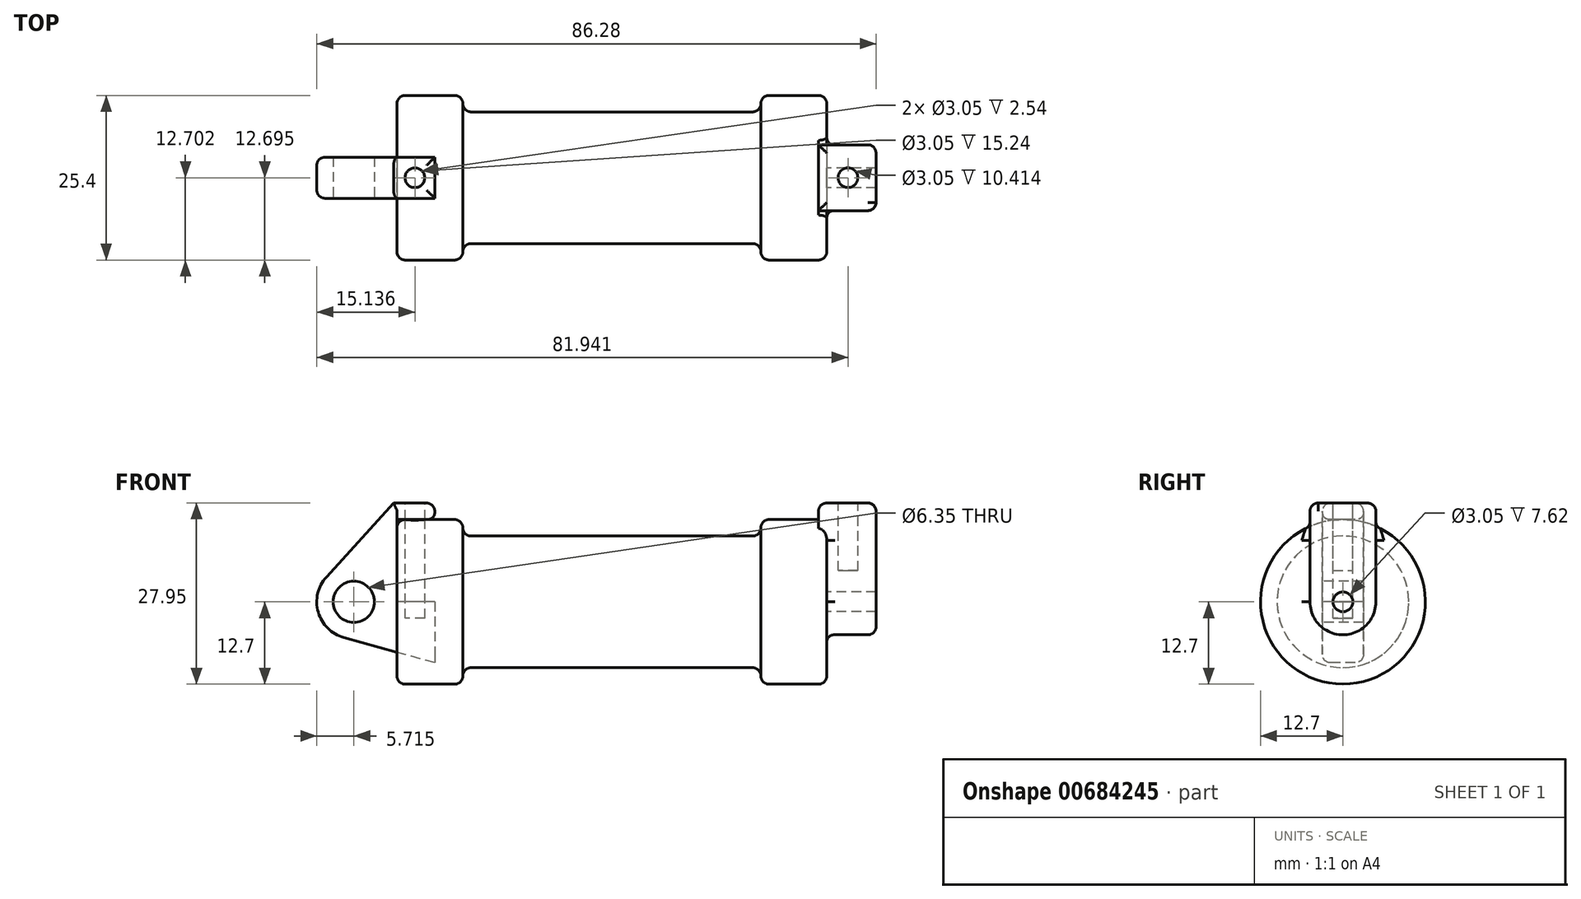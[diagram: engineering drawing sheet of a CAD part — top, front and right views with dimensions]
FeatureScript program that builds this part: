
annotation { "Feature Type Name" : "Feature", "Feature Type Description" : "" }
export const myFeature = defineFeature(function(context is Context, id is Id, definition is map)
    precondition{}
    {
        {
            var Q0;
            Q0=qCreatedBy(makeId("Front.planeOp"),FACE);
            var sketch = newSketch(context, id + "F0", { "sketchPlane" : qUnion([Q0])});
            skLineSegment(sketch, "E0", {"start": v(0, 0) * mm, "end": v(0, 12.7) * mm});
            skLineSegment(sketch, "E1", {"start": v(0, 12.7) * mm, "end": v(10.16, 12.7) * mm});
            skLineSegment(sketch, "E2", {"start": v(10.16, 12.7) * mm, "end": v(10.16, 10.16) * mm});
            skLineSegment(sketch, "E3", {"start": v(10.16, 10.16) * mm, "end": v(56.13, 10.16) * mm});
            skLineSegment(sketch, "E4", {"start": v(56.13, 10.16) * mm, "end": v(56.13, 12.7) * mm});
            skLineSegment(sketch, "E5", {"start": v(56.13, 12.7) * mm, "end": v(66.3, 12.7) * mm});
            skLineSegment(sketch, "E6", {"start": v(66.3, 12.7) * mm, "end": v(66.3, 0) * mm});
            skLineSegment(sketch, "E7", {"start": v(66.3, 0) * mm, "end": v(0, 0) * mm});
            skLineSegment(sketch, "E8", {"start": v(5.84, 15.24) * mm, "end": v(-0.5, 15.24) * mm});
            skLineSegment(sketch, "E9", {"start": v(-0.5, 15.24) * mm, "end": v(-10.88, 3.85) * mm});
            skLineSegment(sketch, "E10", {"start": v(0, 0) * mm, "end": v(-6.65, 0) * mm});
            skCircle(sketch, "E11", {"center": v(-6.65, 0) * mm, "radius": 5.72 * mm});
            skCircle(sketch, "E12", {"center": v(-6.65, 0) * mm, "radius": 3.18 * mm});
            skLineSegment(sketch, "E13", {"start": v(5.84, 15.24) * mm, "end": v(5.84, -9.4) * mm});
            skLineSegment(sketch, "E14", {"start": v(5.84, -9.4) * mm, "end": v(-8.18, -5.5) * mm});
            skSolve(sketch);
        }
        {
            var Q0;
            {var subQ0=sQuery(id+"F0.wireOp",EDGE,"E2");Q0=makeQuery(id+"F0.imprint","IMPRINT",FACE,{"disambiguationData":[TD([[makeQuery(id+"F0.imprint","IMPRINT",EDGE,{"derivedFrom":subQ0}),-1.0]])]});}
            var Q1;
            {var subQ0=sQuery(id+"F0.wireOp",EDGE,"E0");Q1=makeQuery(id+"F0.imprint","IMPRINT",FACE,{"disambiguationData":[TD([[makeQuery(id+"F0.imprint","IMPRINT",EDGE,{"derivedFrom":subQ0}),-1.0]])]});}
            var Q2;
            Q2=sQuery(id+"F0.wireOp",EDGE,"E7");
            revolve(context, id + "F1", {"entities" : qUnion([Q0, Q1]), "axis" : qUnion([Q2]), "revolveType" : RevolveType.FULL});
        }
        {
            var Q0;
            {var subQ1=sQuery(id+"F0.wireOp",EDGE,"E0");Q0=makeQuery(id+"F0.imprint","IMPRINT",FACE,{"disambiguationData":[TD([[makeQuery(id+"F0.imprint","IMPRINT",EDGE,{"derivedFrom":subQ1}),1.0]])]});}
            var Q1;
            {var subQ0=sQuery(id+"F0.wireOp",EDGE,"E14");Q1=makeQuery(id+"F0.imprint","IMPRINT",FACE,{"disambiguationData":[TD([[makeQuery(id+"F0.imprint","IMPRINT",EDGE,{"derivedFrom":subQ0}),-1.0]])]});}
            var Q2;
            {var subQ5=sQuery(id+"F0.wireOp",EDGE,"E12");Q2=makeQuery(id+"F0.imprint","IMPRINT",FACE,{"disambiguationData":[TD([[makeQuery(id+"F0.imprint","IMPRINT",EDGE,{"derivedFrom":subQ5}),-1.0]])]});}
            extrude(context, id + "F2", {"entities" : qUnion([Q0, Q1, Q2]), "endBound" : BoundingType.SYMMETRIC, "oppositeDirection" : true, "depth" : 6.35 * mm, "offsetDistance" : 25.4 * mm});
        }
        {
            var Q0;
            Q0=makeQuery(id+"F1.opRevolve","SWEPT_FACE",FACE,{"disambiguationData":[OSD([sQuery(id+"F0.wireOp",EDGE,"E6")])]});
            var sketch = newSketch(context, id + "F3", { "sketchPlane" : qUnion([Q0])});
            skCircle(sketch, "E15", {"center": v(0, 0) * mm, "radius": 5.08 * mm});
            skCircle(sketch, "E16", {"center": v(0, 0) * mm, "radius": 1.52 * mm});
            skLineSegment(sketch, "E17", {"start": v(-5.08, 0.01) * mm, "end": v(-5.08, 15.25) * mm});
            skLineSegment(sketch, "E18", {"start": v(5.08, 0) * mm, "end": v(5.08, 15.24) * mm});
            skLineSegment(sketch, "E19", {"start": v(5.08, 15.24) * mm, "end": v(-5.08, 15.25) * mm});
            skSolve(sketch);
        }
        {
            var Q0;
            {var subQ0=sQuery(id+"F3.wireOp",EDGE,"E19");Q0=makeQuery(id+"F3.imprint","IMPRINT",FACE,{"disambiguationData":[TD([[makeQuery(id+"F3.imprint","IMPRINT",EDGE,{"derivedFrom":subQ0}),1.0]])]});}
            var Q1;
            {var subQ0=sQuery(id+"F3.wireOp",EDGE,"E17");var subQ1=sQuery(id+"F3.wireOp",EDGE,"E15");var subQ2=makeQuery(id+"F3.imprint","INTERSECT",VERTEX,{"derivedFrom":[subQ1,subQ0]});Q1=makeQuery(id+"F3.imprint","IMPRINT",FACE,{"disambiguationData":[TD([[makeQuery(id+"F3.imprint","IMPRINT",EDGE,{"disambiguationData":[TD([[subQ2,1.0]])],"derivedFrom":subQ1}),-1.0]])]});}
            var Q2;
            Q2=makeQuery(id+"F3.imprint","IMPRINT",FACE,{"disambiguationData":[TD([[makeQuery(id+"F3.imprint","IMPRINT",EDGE,{"derivedFrom":sQuery(id+"F3.wireOp",EDGE,"E16")}),-1.0]])]});
            extrude(context, id + "F4", {"entities" : qUnion([Q0, Q1, Q2]), "operationType" : NewBodyOperationType.ADD, "depth" : 7.62 * mm, "offsetDistance" : 25.4 * mm, "hasSecondDirection" : true, "secondDirectionOppositeDirection" : true, "secondDirectionDepth" : 1.27 * mm});
        }
        {
            var Q0;
            Q0=makeQuery(id+"F2.opExtrude","SWEPT_FACE",FACE,{"disambiguationData":[OSD([sQuery(id+"F0.wireOp",EDGE,"E8")])]});
            var sketch = newSketch(context, id + "F5", { "sketchPlane" : qUnion([Q0])});
            skCircle(sketch, "E20", {"center": v(2.77, 0) * mm, "radius": 1.52 * mm});
            skSolve(sketch);
        }
        {
            var Q0;
            Q0=makeQuery(id+"F5.imprint","IMPRINT",FACE,{"disambiguationData":[TD([[makeQuery(id+"F5.imprint","IMPRINT",EDGE,{"derivedFrom":sQuery(id+"F5.wireOp",EDGE,"E20")}),1.0]])]});
            extrude(context, id + "F6", {"entities" : qUnion([Q0]), "operationType" : NewBodyOperationType.REMOVE, "oppositeDirection" : true, "depth" : 17.78 * mm, "offsetDistance" : 25.4 * mm});
        }
        {
            var Q0;
            Q0=makeQuery(id+"F4.opExtrude","SWEPT_FACE",FACE,{"disambiguationData":[OSD([sQuery(id+"F3.wireOp",EDGE,"E19")])]});
            var sketch = newSketch(context, id + "F7", { "sketchPlane" : qUnion([Q0])});
            skCircle(sketch, "E21", {"center": v(69.57, -0.01) * mm, "radius": 1.52 * mm});
            skSolve(sketch);
        }
        {
            var Q0;
            Q0=makeQuery(id+"F7.imprint","IMPRINT",FACE,{"disambiguationData":[TD([[makeQuery(id+"F7.imprint","IMPRINT",EDGE,{"derivedFrom":sQuery(id+"F7.wireOp",EDGE,"E21")}),1.0]])]});
            extrude(context, id + "F8", {"entities" : qUnion([Q0]), "operationType" : NewBodyOperationType.REMOVE, "oppositeDirection" : true, "depth" : 10.4 * mm, "offsetDistance" : 25.4 * mm});
        }
        {
            var Q0;
            Q0=makeQuery(id+"F4.opExtrude","CAP_EDGE",EDGE,{"disambiguationData":[OSD([sQuery(id+"F3.wireOp",EDGE,"E19")])],"isStart":false});
            var Q1;
            Q1=makeQuery(id+"F4.opExtrude","SWEPT_EDGE",EDGE,{"disambiguationData":[OSD([sQuery(id+"F3.wireOp",EDGE,"E17"),sQuery(id+"F3.wireOp",EDGE,"E19")])]});
            var Q2;
            Q2=makeQuery(id+"F4.opExtrude","CAP_EDGE",EDGE,{"disambiguationData":[OSD([sQuery(id+"F3.wireOp",EDGE,"E17")])],"isStart":false});
            var Q3;
            Q3=makeQuery(id+"F4.opExtrude","CAP_EDGE",EDGE,{"disambiguationData":[OSD([sQuery(id+"F3.wireOp",EDGE,"E15")])],"isStart":false});
            var Q4;
            Q4=makeQuery(id+"F4.opExtrude","SWEPT_EDGE",EDGE,{"disambiguationData":[OSD([sQuery(id+"F3.wireOp",EDGE,"E18"),sQuery(id+"F3.wireOp",EDGE,"E19")])]});
            var Q5;
            Q5=makeQuery(id+"F4.opExtrude","CAP_EDGE",EDGE,{"disambiguationData":[OSD([sQuery(id+"F3.wireOp",EDGE,"E18")])],"isStart":false});
            var Q6;
            Q6=makeQuery(id+"F4.opExtrude","CAP_EDGE",EDGE,{"disambiguationData":[OSD([sQuery(id+"F3.wireOp",EDGE,"E19")])],"isStart":true});
            var Q7;
            Q7=makeQuery(id+"F1.opRevolve","SWEPT_EDGE",EDGE,{"disambiguationData":[OSD([sQuery(id+"F0.wireOp",EDGE,"E4"),sQuery(id+"F0.wireOp",EDGE,"E5")])]});
            var Q8;
            Q8=makeQuery(id+"F1.opRevolve","SWEPT_EDGE",EDGE,{"disambiguationData":[OSD([sQuery(id+"F0.wireOp",EDGE,"E5"),sQuery(id+"F0.wireOp",EDGE,"E6")])]});
            var Q9;
            Q9=makeQuery(id+"F1.opRevolve","SWEPT_EDGE",EDGE,{"disambiguationData":[OSD([sQuery(id+"F0.wireOp",EDGE,"E1"),sQuery(id+"F0.wireOp",EDGE,"E2")])]});
            var Q10;
            Q10=makeQuery(id+"F1.opRevolve","SWEPT_EDGE",EDGE,{"disambiguationData":[OSD([sQuery(id+"F0.wireOp",EDGE,"E0"),sQuery(id+"F0.wireOp",EDGE,"E1")])]});
            var Q11;
            Q11=makeQuery(id+"F2.opExtrude","CAP_EDGE",EDGE,{"disambiguationData":[OSD([sQuery(id+"F0.wireOp",EDGE,"E9")])],"isStart":true});
            var Q12;
            Q12=makeQuery(id+"F2.opExtrude","CAP_EDGE",EDGE,{"disambiguationData":[OSD([sQuery(id+"F0.wireOp",EDGE,"E9")])],"isStart":false});
            var Q13;
            Q13=makeQuery(id+"F2.opExtrude","CAP_EDGE",EDGE,{"disambiguationData":[OSD([sQuery(id+"F0.wireOp",EDGE,"E8")])],"isStart":false});
            var Q14;
            Q14=makeQuery(id+"F2.opExtrude","SWEPT_EDGE",EDGE,{"disambiguationData":[OSD([sQuery(id+"F0.wireOp",EDGE,"E8"),sQuery(id+"F0.wireOp",EDGE,"E13")])]});
            var Q15;
            Q15=makeQuery(id+"F2.opExtrude","CAP_EDGE",EDGE,{"disambiguationData":[OSD([sQuery(id+"F0.wireOp",EDGE,"E8")])],"isStart":true});
            var Q16;
            Q16=makeQuery(id+"F1.opRevolve","SWEPT_FACE",FACE,{"disambiguationData":[OSD([sQuery(id+"F0.wireOp",EDGE,"E3")])]});
            fillet(context, id + "F9", {"entities" : qUnion([Q0, Q1, Q2, Q3, Q4, Q5, Q6, Q7, Q8, Q9, Q10, Q11, Q12, Q13, Q14, Q15, Q16]), "radius" : 1.27 * mm, "tangentPropagation" : true, "allowEdgeOverflow" : false});
        }
        {
            var Q0;
            Q0=makeQuery(id+"F2.opExtrude","CAP_EDGE",EDGE,{"disambiguationData":[OSD([sQuery(id+"F0.wireOp",EDGE,"E1")])],"isStart":false});
            var Q1;
            Q1=makeQuery(id+"F1.opRevolve","SWEPT_FACE",FACE,{"disambiguationData":[OSD([sQuery(id+"F0.wireOp",EDGE,"E0")])]});
            var Q2;
            Q2=makeQuery(id+"F2.opExtrude","CAP_EDGE",EDGE,{"disambiguationData":[OSD([sQuery(id+"F0.wireOp",EDGE,"E1")])],"isStart":true});
            var Q3;
            Q3=makeQuery(id+"F2.opExtrude","SWEPT_EDGE",EDGE,{"disambiguationData":[OSD([sQuery(id+"F0.wireOp",EDGE,"E1"),sQuery(id+"F0.wireOp",EDGE,"E13")])]});
            var Q4;
            Q4=makeQuery(id+"F4.boolean.opBoolean","INTERSECT",EDGE,{"derivedFrom":[makeQuery(id+"F1.opRevolve","SWEPT_FACE",FACE,{"disambiguationData":[OSD([sQuery(id+"F0.wireOp",EDGE,"E6")])]}),makeQuery(id+"F4.opExtrude","SWEPT_FACE",FACE,{"disambiguationData":[OSD([sQuery(id+"F3.wireOp",EDGE,"E17")])]})]});
            var Q5;
            Q5=makeQuery(id+"F4.boolean.opBoolean","INTERSECT",EDGE,{"derivedFrom":[makeQuery(id+"F1.opRevolve","SWEPT_FACE",FACE,{"disambiguationData":[OSD([sQuery(id+"F0.wireOp",EDGE,"E6")])]}),makeQuery(id+"F4.opExtrude","SWEPT_FACE",FACE,{"disambiguationData":[OSD([sQuery(id+"F3.wireOp",EDGE,"E15")])]})]});
            var Q6;
            Q6=makeQuery(id+"F4.boolean.opBoolean","INTERSECT",EDGE,{"derivedFrom":[makeQuery(id+"F1.opRevolve","SWEPT_FACE",FACE,{"disambiguationData":[OSD([sQuery(id+"F0.wireOp",EDGE,"E6")])]}),makeQuery(id+"F4.opExtrude","SWEPT_FACE",FACE,{"disambiguationData":[OSD([sQuery(id+"F3.wireOp",EDGE,"E18")])]})]});
            fillet(context, id + "F10", {"entities" : qUnion([Q0, Q1, Q2, Q3, Q4, Q5, Q6]), "radius" : 1.27 * mm, "tangentPropagation" : true, "rho" : 0.5, "crossSection" : FilletCrossSection.CONIC, "allowEdgeOverflow" : false});
        }
    });
